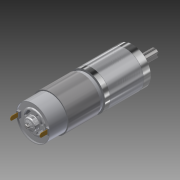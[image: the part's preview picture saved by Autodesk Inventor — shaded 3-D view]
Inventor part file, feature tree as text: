
AUTODESK INVENTOR PART (.ipt)
format: ipt  version: 2016 SP1 (Build 200210100, 210)  size: 342,016 bytes
history: native  units: in
note: dims shown in document units (in); Inventor stores cm internally (conversion verified against a paired STEP export)
features: mirror x1, other x1, imported_body x1
ambient origin geometry x8: Origin, YZ Plane, XZ Plane, XY Plane, X Axis, Y Axis, Z Axis, Center Point
bodies: Body1 (feature_tree)
feature tree (3):
  mirror  "Mirror2"
  other  "PG-71"
  imported_body  "Base1"
